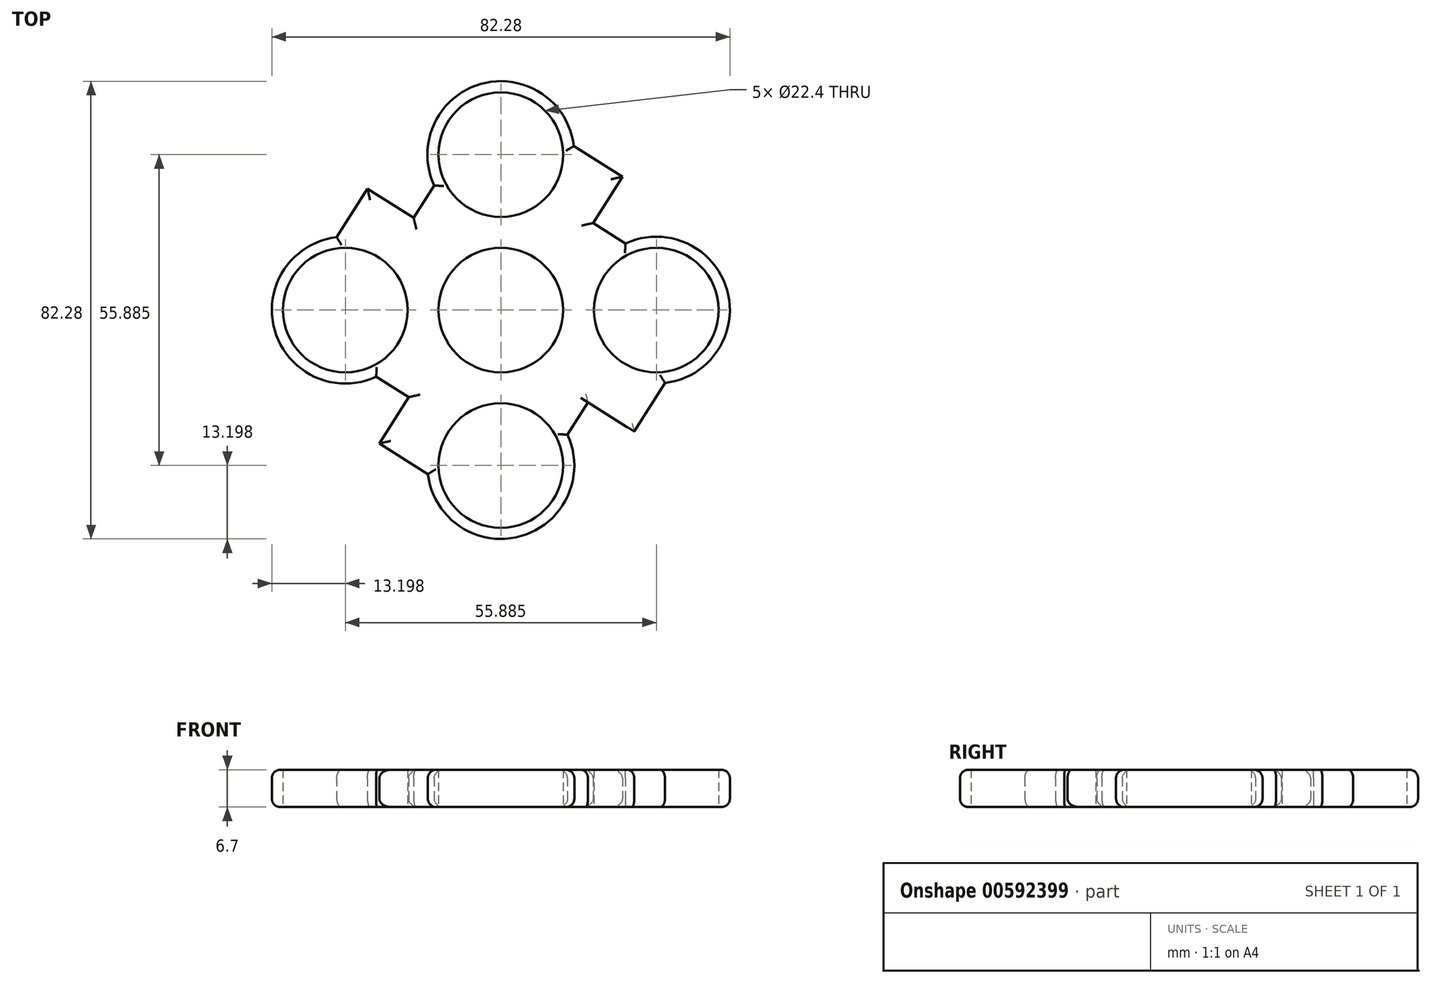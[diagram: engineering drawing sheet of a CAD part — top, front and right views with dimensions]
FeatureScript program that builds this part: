
annotation { "Feature Type Name" : "Feature", "Feature Type Description" : "" }
export const myFeature = defineFeature(function(context is Context, id is Id, definition is map)
    precondition{}
    {
        {
            var Q0;
            Q0=qCreatedBy(makeId("Top.planeOp"),FACE);
            var sketch = newSketch(context, id + "F0", { "sketchPlane" : qUnion([Q0])});
            skCircle(sketch, "E0", {"center": v(0, 0) * mm, "radius": 11.2 * mm});
            skCircle(sketch, "E1", {"center": v(0, 27.94) * mm, "radius": 11.2 * mm});
            skArc(sketch, "E2", {"start": v(13.1, 29.49) * mm, "mid": v(-3.59, 40.65) * mm, "end": v(-11.98, 22.4) * mm});
            skCircle(sketch, "E3.1.0", {"center": v(-27.94, 0) * mm, "radius": 11.2 * mm});
            skArc(sketch, "E3.1.1", {"start": v(-29.49, 13.1) * mm, "mid": v(-40.65, -3.59) * mm, "end": v(-22.4, -11.98) * mm});
            skCircle(sketch, "E3.2.0", {"center": v(0, -27.94) * mm, "radius": 11.2 * mm});
            skArc(sketch, "E3.2.1", {"start": v(-13.1, -29.49) * mm, "mid": v(3.59, -40.65) * mm, "end": v(11.98, -22.4) * mm});
            skCircle(sketch, "E3.3.0", {"center": v(27.94, 0) * mm, "radius": 11.2 * mm});
            skArc(sketch, "E3.3.1", {"start": v(29.49, -13.1) * mm, "mid": v(40.65, 3.59) * mm, "end": v(22.4, 11.98) * mm});
            skLineSegment(sketch, "E4", {"start": v(13.1, 29.49) * mm, "end": v(21.83, 23.97) * mm});
            skLineSegment(sketch, "E5", {"start": v(21.83, 23.97) * mm, "end": v(16.58, 15.66) * mm});
            skLineSegment(sketch, "E6", {"start": v(16.58, 15.66) * mm, "end": v(22.4, 11.98) * mm});
            skLineSegment(sketch, "E7.1.0", {"start": v(-29.49, 13.1) * mm, "end": v(-23.97, 21.83) * mm});
            skLineSegment(sketch, "E7.1.1", {"start": v(-23.97, 21.83) * mm, "end": v(-15.66, 16.58) * mm});
            skLineSegment(sketch, "E7.1.2", {"start": v(-15.66, 16.58) * mm, "end": v(-11.98, 22.4) * mm});
            skLineSegment(sketch, "E7.2.0", {"start": v(-13.1, -29.49) * mm, "end": v(-21.83, -23.97) * mm});
            skLineSegment(sketch, "E7.2.1", {"start": v(-21.83, -23.97) * mm, "end": v(-16.58, -15.66) * mm});
            skLineSegment(sketch, "E7.2.2", {"start": v(-16.58, -15.66) * mm, "end": v(-22.4, -11.98) * mm});
            skLineSegment(sketch, "E7.3.0", {"start": v(29.49, -13.1) * mm, "end": v(23.97, -21.83) * mm});
            skLineSegment(sketch, "E7.3.1", {"start": v(23.97, -21.83) * mm, "end": v(15.66, -16.58) * mm});
            skLineSegment(sketch, "E7.3.2", {"start": v(15.66, -16.58) * mm, "end": v(11.98, -22.4) * mm});
            skSolve(sketch);
        }
        {
            var Q0;
            Q0 = qSketchRegion(id + "F0", true);
            extrude(context, id + "F1", {"entities" : qUnion([Q0]), "depth" : 6.7 * mm, "offsetDistance" : 25 * mm});
        }
        {
            var Q0;
            Q0=makeQuery(id+"F1.opExtrude","CAP_EDGE",EDGE,{"disambiguationData":[OSD([sQuery(id+"F0.wireOp",EDGE,"E4")])],"isStart":false});
            var Q1;
            Q1=makeQuery(id+"F1.opExtrude","CAP_EDGE",EDGE,{"disambiguationData":[OSD([sQuery(id+"F0.wireOp",EDGE,"E2")])],"isStart":false});
            var Q2;
            Q2=makeQuery(id+"F1.opExtrude","CAP_EDGE",EDGE,{"disambiguationData":[OSD([sQuery(id+"F0.wireOp",EDGE,"E6")])],"isStart":false});
            var Q3;
            Q3=makeQuery(id+"F1.opExtrude","CAP_EDGE",EDGE,{"disambiguationData":[OSD([sQuery(id+"F0.wireOp",EDGE,"E5")])],"isStart":false});
            var Q4;
            Q4=makeQuery(id+"F1.opExtrude","CAP_EDGE",EDGE,{"disambiguationData":[OSD([sQuery(id+"F0.wireOp",EDGE,"E3.3.1")])],"isStart":false});
            var Q5;
            Q5=makeQuery(id+"F1.opExtrude","CAP_EDGE",EDGE,{"disambiguationData":[OSD([sQuery(id+"F0.wireOp",EDGE,"E7.3.0")])],"isStart":false});
            var Q6;
            Q6=makeQuery(id+"F1.opExtrude","CAP_EDGE",EDGE,{"disambiguationData":[OSD([sQuery(id+"F0.wireOp",EDGE,"E7.3.2")])],"isStart":false});
            var Q7;
            Q7=makeQuery(id+"F1.opExtrude","CAP_EDGE",EDGE,{"disambiguationData":[OSD([sQuery(id+"F0.wireOp",EDGE,"E3.2.1")])],"isStart":false});
            var Q8;
            Q8=makeQuery(id+"F1.opExtrude","CAP_EDGE",EDGE,{"disambiguationData":[OSD([sQuery(id+"F0.wireOp",EDGE,"E7.2.0")])],"isStart":false});
            var Q9;
            Q9=makeQuery(id+"F1.opExtrude","CAP_EDGE",EDGE,{"disambiguationData":[OSD([sQuery(id+"F0.wireOp",EDGE,"E7.2.2")])],"isStart":false});
            var Q10;
            Q10=makeQuery(id+"F1.opExtrude","CAP_EDGE",EDGE,{"disambiguationData":[OSD([sQuery(id+"F0.wireOp",EDGE,"E7.2.1")])],"isStart":false});
            var Q11;
            Q11=makeQuery(id+"F1.opExtrude","CAP_EDGE",EDGE,{"disambiguationData":[OSD([sQuery(id+"F0.wireOp",EDGE,"E3.1.1")])],"isStart":false});
            var Q12;
            Q12=makeQuery(id+"F1.opExtrude","CAP_EDGE",EDGE,{"disambiguationData":[OSD([sQuery(id+"F0.wireOp",EDGE,"E7.1.0")])],"isStart":false});
            var Q13;
            Q13=makeQuery(id+"F1.opExtrude","CAP_EDGE",EDGE,{"disambiguationData":[OSD([sQuery(id+"F0.wireOp",EDGE,"E7.1.2")])],"isStart":false});
            var Q14;
            Q14=makeQuery(id+"F1.opExtrude","CAP_EDGE",EDGE,{"disambiguationData":[OSD([sQuery(id+"F0.wireOp",EDGE,"E7.1.1")])],"isStart":false});
            fillet(context, id + "F2", {"entities" : qUnion([Q0, Q1, Q2, Q3, Q4, Q5, Q6, Q7, Q8, Q9, Q10, Q11, Q12, Q13, Q14]), "radius" : 1.5 * mm, "tangentPropagation" : true, "allowEdgeOverflow" : false});
        }
        {
            var Q0;
            Q0=makeQuery(id+"F1.opExtrude","CAP_EDGE",EDGE,{"disambiguationData":[OSD([sQuery(id+"F0.wireOp",EDGE,"E3.2.1")])],"isStart":true});
            var Q1;
            Q1=makeQuery(id+"F1.opExtrude","CAP_EDGE",EDGE,{"disambiguationData":[OSD([sQuery(id+"F0.wireOp",EDGE,"E7.3.2")])],"isStart":true});
            var Q2;
            Q2=makeQuery(id+"F1.opExtrude","CAP_EDGE",EDGE,{"disambiguationData":[OSD([sQuery(id+"F0.wireOp",EDGE,"E7.3.1")])],"isStart":true});
            var Q3;
            Q3=makeQuery(id+"F1.opExtrude","CAP_EDGE",EDGE,{"disambiguationData":[OSD([sQuery(id+"F0.wireOp",EDGE,"E3.3.1")])],"isStart":true});
            var Q4;
            Q4=makeQuery(id+"F1.opExtrude","CAP_EDGE",EDGE,{"disambiguationData":[OSD([sQuery(id+"F0.wireOp",EDGE,"E7.3.0")])],"isStart":true});
            var Q5;
            Q5=makeQuery(id+"F1.opExtrude","CAP_EDGE",EDGE,{"disambiguationData":[OSD([sQuery(id+"F0.wireOp",EDGE,"E6")])],"isStart":true});
            var Q6;
            Q6=makeQuery(id+"F1.opExtrude","CAP_EDGE",EDGE,{"disambiguationData":[OSD([sQuery(id+"F0.wireOp",EDGE,"E5")])],"isStart":true});
            var Q7;
            Q7=makeQuery(id+"F1.opExtrude","CAP_EDGE",EDGE,{"disambiguationData":[OSD([sQuery(id+"F0.wireOp",EDGE,"E4")])],"isStart":true});
            var Q8;
            Q8=makeQuery(id+"F1.opExtrude","CAP_EDGE",EDGE,{"disambiguationData":[OSD([sQuery(id+"F0.wireOp",EDGE,"E2")])],"isStart":true});
            var Q9;
            Q9=makeQuery(id+"F1.opExtrude","CAP_EDGE",EDGE,{"disambiguationData":[OSD([sQuery(id+"F0.wireOp",EDGE,"E7.1.2")])],"isStart":true});
            var Q10;
            Q10=makeQuery(id+"F1.opExtrude","CAP_EDGE",EDGE,{"disambiguationData":[OSD([sQuery(id+"F0.wireOp",EDGE,"E7.1.1")])],"isStart":true});
            var Q11;
            Q11=makeQuery(id+"F1.opExtrude","CAP_EDGE",EDGE,{"disambiguationData":[OSD([sQuery(id+"F0.wireOp",EDGE,"E7.1.0")])],"isStart":true});
            var Q12;
            Q12=makeQuery(id+"F1.opExtrude","CAP_EDGE",EDGE,{"disambiguationData":[OSD([sQuery(id+"F0.wireOp",EDGE,"E3.1.1")])],"isStart":true});
            var Q13;
            Q13=makeQuery(id+"F1.opExtrude","CAP_EDGE",EDGE,{"disambiguationData":[OSD([sQuery(id+"F0.wireOp",EDGE,"E7.2.2")])],"isStart":true});
            var Q14;
            Q14=makeQuery(id+"F1.opExtrude","CAP_EDGE",EDGE,{"disambiguationData":[OSD([sQuery(id+"F0.wireOp",EDGE,"E7.2.1")])],"isStart":true});
            var Q15;
            Q15=makeQuery(id+"F1.opExtrude","CAP_EDGE",EDGE,{"disambiguationData":[OSD([sQuery(id+"F0.wireOp",EDGE,"E7.2.0")])],"isStart":true});
            fillet(context, id + "F3", {"entities" : qUnion([Q0, Q1, Q2, Q3, Q4, Q5, Q6, Q7, Q8, Q9, Q10, Q11, Q12, Q13, Q14, Q15]), "radius" : 1.5 * mm, "tangentPropagation" : true, "allowEdgeOverflow" : false});
        }
    });
